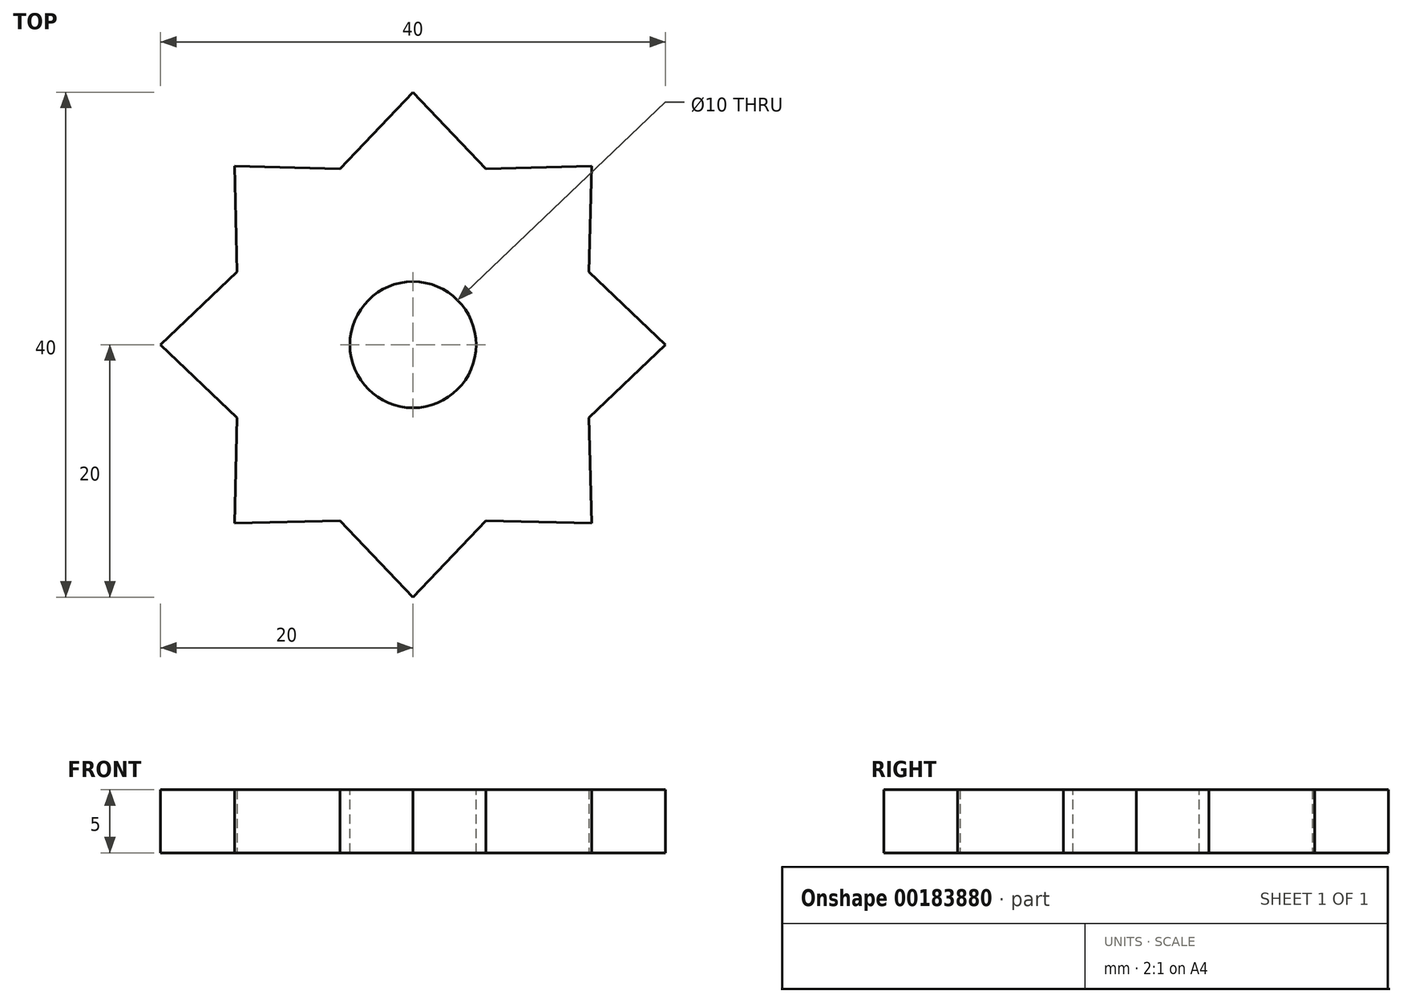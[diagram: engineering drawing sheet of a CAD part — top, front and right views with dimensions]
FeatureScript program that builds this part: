
annotation { "Feature Type Name" : "Feature", "Feature Type Description" : "" }
export const myFeature = defineFeature(function(context is Context, id is Id, definition is map)
    precondition{}
    {
        {
            var Q0;
            Q0=qCreatedBy(makeId("Top.planeOp"),FACE);
            var sketch = newSketch(context, id + "F0", { "sketchPlane" : qUnion([Q0])});
            skCircle(sketch, "E0", {"center": v(0, 0) * mm, "radius": 15 * mm});
            skLineSegment(sketch, "E1", {"start": v(0, 0) * mm, "end": v(0, 15) * mm, "construction": true});
            skLineSegment(sketch, "E2", {"start": v(0, 15) * mm, "end": v(0, 20) * mm});
            skLineSegment(sketch, "E3", {"start": v(0, 20) * mm, "end": v(5.94, 13.78) * mm});
            skLineSegment(sketch, "E4.MirrorCS", {"start": v(0, 20) * mm, "end": v(-5.94, 13.78) * mm});
            skLineSegment(sketch, "E5.1.0", {"start": v(-14.14, 14.14) * mm, "end": v(-13.94, 5.54) * mm});
            skLineSegment(sketch, "E5.1.1", {"start": v(-14.14, 14.14) * mm, "end": v(-5.54, 13.94) * mm});
            skLineSegment(sketch, "E5.2.0", {"start": v(-20, 0) * mm, "end": v(-13.78, -5.94) * mm});
            skLineSegment(sketch, "E5.2.1", {"start": v(-20, 0) * mm, "end": v(-13.78, 5.94) * mm});
            skLineSegment(sketch, "E5.3.0", {"start": v(-14.14, -14.14) * mm, "end": v(-5.54, -13.94) * mm});
            skLineSegment(sketch, "E5.3.1", {"start": v(-14.14, -14.14) * mm, "end": v(-13.94, -5.54) * mm});
            skLineSegment(sketch, "E5.4.0", {"start": v(0, -20) * mm, "end": v(5.94, -13.78) * mm});
            skLineSegment(sketch, "E5.4.1", {"start": v(0, -20) * mm, "end": v(-5.94, -13.78) * mm});
            skLineSegment(sketch, "E5.5.0", {"start": v(14.14, -14.14) * mm, "end": v(13.94, -5.54) * mm});
            skLineSegment(sketch, "E5.5.1", {"start": v(14.14, -14.14) * mm, "end": v(5.54, -13.94) * mm});
            skLineSegment(sketch, "E5.6.0", {"start": v(20, 0) * mm, "end": v(13.78, 5.94) * mm});
            skLineSegment(sketch, "E5.6.1", {"start": v(20, 0) * mm, "end": v(13.78, -5.94) * mm});
            skLineSegment(sketch, "E5.7.0", {"start": v(14.14, 14.14) * mm, "end": v(5.54, 13.94) * mm});
            skLineSegment(sketch, "E5.7.1", {"start": v(14.14, 14.14) * mm, "end": v(13.94, 5.54) * mm});
            skSolve(sketch);
        }
        {
            var Q0;
            Q0=qSketchRegion(id+"F0",true);
            var Q1;
            {var subQ0=sQuery(id+"F0.wireOp",EDGE,"E0");var subQ3=makeQuery(id+"F0.imprint","INTERSECT",VERTEX,{"derivedFrom":[subQ0,sQuery(id+"F0.wireOp",EDGE,"E5.6.0")]});Q1=makeQuery(id+"F0.imprint","IMPRINT",FACE,{"disambiguationData":[TD([[makeQuery(id+"F0.imprint","IMPRINT",EDGE,{"disambiguationData":[TD([[subQ3,1.0]])],"derivedFrom":subQ0}),1.0]])]});}
            extrude(context, id + "F1", {"entities" : qUnion([Q0, Q1]), "depth" : 5 * mm});
        }
        {
            var Q0;
            Q0=makeQuery(id+"F1.opExtrude","CAP_FACE",FACE,{"disambiguationData":[OSD([sQuery(id+"F0.wireOp",EDGE,"E3"),sQuery(id+"F0.wireOp",EDGE,"E4.MirrorCS"),sQuery(id+"F0.wireOp",EDGE,"E5.1.0"),sQuery(id+"F0.wireOp",EDGE,"E5.1.1"),sQuery(id+"F0.wireOp",EDGE,"E5.2.0"),sQuery(id+"F0.wireOp",EDGE,"E5.2.1"),sQuery(id+"F0.wireOp",EDGE,"E5.3.0"),sQuery(id+"F0.wireOp",EDGE,"E5.3.1"),sQuery(id+"F0.wireOp",EDGE,"E5.4.0"),sQuery(id+"F0.wireOp",EDGE,"E5.4.1"),sQuery(id+"F0.wireOp",EDGE,"E5.5.0"),sQuery(id+"F0.wireOp",EDGE,"E5.5.1"),sQuery(id+"F0.wireOp",EDGE,"E5.6.0"),sQuery(id+"F0.wireOp",EDGE,"E5.6.1"),sQuery(id+"F0.wireOp",EDGE,"E5.7.0"),sQuery(id+"F0.wireOp",EDGE,"E5.7.1")])],"isStart":false});
            var sketch = newSketch(context, id + "F2", { "sketchPlane" : qUnion([Q0])});
            skCircle(sketch, "E6", {"center": v(0, 0) * mm, "radius": 5 * mm});
            skSolve(sketch);
        }
        {
            var Q0;
            Q0=qSketchRegion(id+"F2",true);
            extrude(context, id + "F3", {"entities" : qUnion([Q0]), "operationType" : NewBodyOperationType.REMOVE, "oppositeDirection" : true, "depth" : 25 * mm});
        }
    });
